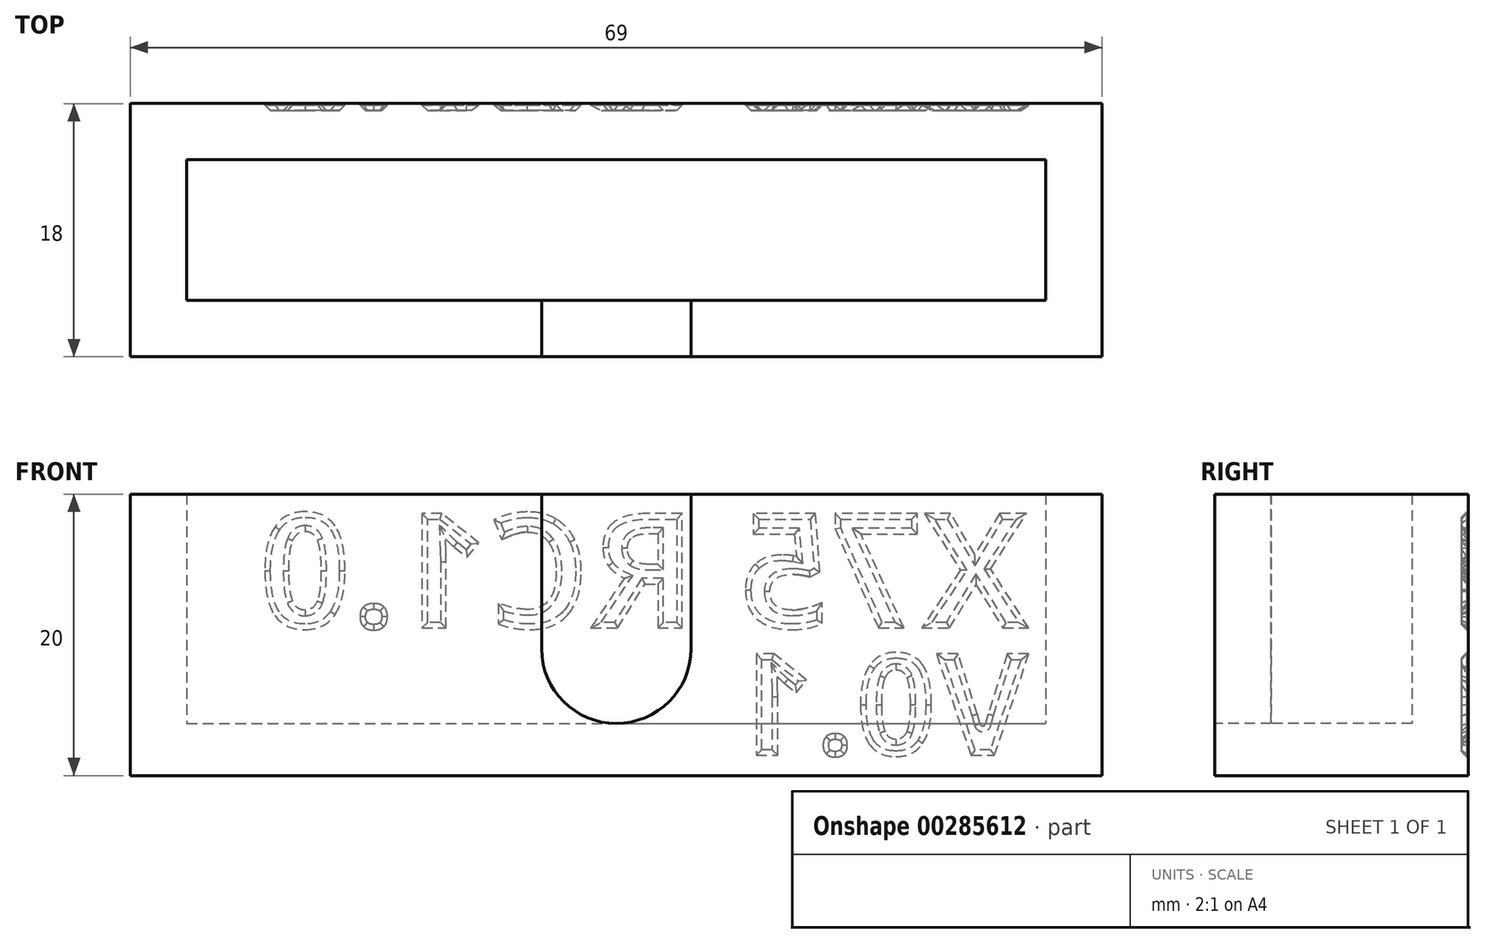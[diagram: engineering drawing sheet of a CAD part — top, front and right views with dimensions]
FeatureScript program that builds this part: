
annotation { "Feature Type Name" : "Feature", "Feature Type Description" : "" }
export const myFeature = defineFeature(function(context is Context, id is Id, definition is map)
    precondition{}
    {
        {
            var Q0;
            Q0=qCreatedBy(makeId("Top.planeOp"),FACE);
            var sketch = newSketch(context, id + "F0", { "sketchPlane" : qUnion([Q0])});
            skLineSegment(sketch, "E0.bottom", {"start": v(-31.49, -9.3) * mm, "end": v(37.51, -9.3) * mm});
            skLineSegment(sketch, "E0.top", {"start": v(-31.49, -27.3) * mm, "end": v(37.51, -27.3) * mm});
            skLineSegment(sketch, "E0.left", {"start": v(-31.49, -9.3) * mm, "end": v(-31.49, -27.3) * mm});
            skLineSegment(sketch, "E0.right", {"start": v(37.51, -9.3) * mm, "end": v(37.51, -27.3) * mm});
            skSolve(sketch);
        }
        {
            var Q0;
            Q0 = qSketchRegion(id + "F0", true);
            extrude(context, id + "F1", {"entities" : qUnion([Q0]), "depth" : 3.7 * mm});
        }
        {
            var Q0;
            Q0=makeQuery(id+"F1.opExtrude","CAP_FACE",FACE,{"disambiguationData":[OSD([sQuery(id+"F0.wireOp",EDGE,"E0.bottom"),sQuery(id+"F0.wireOp",EDGE,"E0.top"),sQuery(id+"F0.wireOp",EDGE,"E0.left"),sQuery(id+"F0.wireOp",EDGE,"E0.right")])],"isStart":false});
            var sketch = newSketch(context, id + "F2", { "sketchPlane" : qUnion([Q0])});
            skLineSegment(sketch, "E1.0.0", {"start": v(-31.49, -9.3) * mm, "end": v(-31.49, -27.3) * mm});
            skLineSegment(sketch, "E1.0.1", {"start": v(-31.49, -27.3) * mm, "end": v(37.51, -27.3) * mm});
            skLineSegment(sketch, "E1.0.2", {"start": v(37.51, -27.3) * mm, "end": v(37.51, -9.3) * mm});
            skLineSegment(sketch, "E1.0.3", {"start": v(37.51, -9.3) * mm, "end": v(-31.49, -9.3) * mm});
            skLineSegment(sketch, "E2.bottom", {"start": v(-27.49, -13.3) * mm, "end": v(33.51, -13.3) * mm});
            skLineSegment(sketch, "E2.top", {"start": v(-27.49, -23.3) * mm, "end": v(33.51, -23.3) * mm});
            skLineSegment(sketch, "E2.left", {"start": v(-27.49, -13.3) * mm, "end": v(-27.49, -23.3) * mm});
            skLineSegment(sketch, "E2.right", {"start": v(33.51, -13.3) * mm, "end": v(33.51, -23.3) * mm});
            skSolve(sketch);
        }
        {
            var Q0;
            Q0 = qSketchRegion(id + "F2", true);
            extrude(context, id + "F3", {"entities" : qUnion([Q0]), "operationType" : NewBodyOperationType.ADD, "depth" : (20 - 3.7) * mm});
        }
        {
            var Q0;
            Q0=makeQuery(id+"F3.boolean.opBoolean","MERGE",FACE,{"derivedFrom":[makeQuery(id+"F1.opExtrude","SWEPT_FACE",FACE,{"disambiguationData":[OSD([sQuery(id+"F0.wireOp",EDGE,"E0.top")])]}),makeQuery(id+"F3.opExtrude","SWEPT_FACE",FACE,{"disambiguationData":[OSD([sQuery(id+"F2.wireOp",EDGE,"E1.0.1")])]})]});
            var sketch = newSketch(context, id + "F4", { "sketchPlane" : qUnion([Q0])});
            skLineSegment(sketch, "E3", {"start": v(-31.49, 20) * mm, "end": v(-2.29, 20) * mm, "construction": true});
            skLineSegment(sketch, "E4", {"start": v(-2.29, 20) * mm, "end": v(8.31, 20) * mm});
            skLineSegment(sketch, "E5", {"start": v(-2.29, 20) * mm, "end": v(-2.29, 9) * mm});
            skLineSegment(sketch, "E6", {"start": v(3.01, 3.7) * mm, "end": v(3.01, 3.7) * mm});
            skLineSegment(sketch, "E7", {"start": v(8.31, 9) * mm, "end": v(8.31, 20) * mm});
            skPoint(sketch, "E8.visualSharp", {"position": v(-2.29, 3.7) * mm});
            skArc(sketch, "E8.filletArc", {"start": v(-2.29, 9) * mm, "mid": v(-0.73, 5.25) * mm, "end": v(3.01, 3.7) * mm});
            skPoint(sketch, "E9.visualSharp", {"position": v(8.31, 3.7) * mm});
            skArc(sketch, "E9.filletArc", {"start": v(3.01, 3.7) * mm, "mid": v(6.76, 5.25) * mm, "end": v(8.31, 9) * mm});
            skSolve(sketch);
        }
        {
            var Q0;
            Q0 = qSketchRegion(id + "F4", true);
            extrude(context, id + "F5", {"entities" : qUnion([Q0]), "operationType" : NewBodyOperationType.REMOVE, "oppositeDirection" : true, "depth" : 5 * mm});
        }
        {
            var Q0;
            Q0=makeQuery(id+"F3.boolean.opBoolean","MERGE",FACE,{"derivedFrom":[makeQuery(id+"F1.opExtrude","SWEPT_FACE",FACE,{"disambiguationData":[OSD([sQuery(id+"F0.wireOp",EDGE,"E0.bottom")])]}),makeQuery(id+"F3.opExtrude","SWEPT_FACE",FACE,{"disambiguationData":[OSD([sQuery(id+"F2.wireOp",EDGE,"E1.0.3")])]})]});
            var sketch = newSketch(context, id + "F6", { "sketchPlane" : qUnion([Q0])});
            skText(sketch, "E10", { "text": "X75 RC1.0 \n", "fontName": "OpenSans-Bold.ttf"});
            skText(sketch, "E11", { "text": "V0.1", "fontName": "OpenSans-Bold.ttf"});
            const initialGuessF6  = {"E10": [-0.0323, 0.01048, 1, 0, 0.00821], "E11": [-0.0323, 0.00144, 1, 0, 0.00726]};
            skSetInitialGuess(sketch, initialGuessF6);
            skSolve(sketch);
        }
        {
            var Q0;
            Q0 = qSketchRegion(id + "F6", true);
            extrude(context, id + "F7", {"entities" : qUnion([Q0]), "operationType" : NewBodyOperationType.REMOVE, "oppositeDirection" : true, "depth" : .5 * mm});
        }
        {
            var Q0;
            Q0=makeQuery(id+"F7.boolean.opBoolean","COPY",EDGE,{"derivedFrom":makeQuery(id+"F7.opExtrude","SWEPT_EDGE",EDGE,{"disambiguationData":[OSD([sQuery(id+"F6.wireOp",EDGE,"E11.sketch_text.stroke-7"),sQuery(id+"F6.wireOp",EDGE,"E11.sketch_text.stroke-8")])]})});
            fillet(context, id + "F8", {"entities" : qUnion([Q0]), "radius" : .2 * mm, "tangentPropagation" : true, "allowEdgeOverflow" : false});
        }
        {
            var Q0;
            Q0=makeQuery(id+"F7.boolean.opBoolean","COPY",FACE,{"derivedFrom":makeQuery(id+"F7.opExtrude","CAP_FACE",FACE,{"disambiguationData":[OSD([sQuery(id+"F6.wireOp",EDGE,"E10.sketch_text.stroke-0"),sQuery(id+"F6.wireOp",EDGE,"E10.sketch_text.stroke-1"),sQuery(id+"F6.wireOp",EDGE,"E10.sketch_text.stroke-2"),sQuery(id+"F6.wireOp",EDGE,"E10.sketch_text.stroke-3"),sQuery(id+"F6.wireOp",EDGE,"E10.sketch_text.stroke-4"),sQuery(id+"F6.wireOp",EDGE,"E10.sketch_text.stroke-5"),sQuery(id+"F6.wireOp",EDGE,"E10.sketch_text.stroke-6"),sQuery(id+"F6.wireOp",EDGE,"E10.sketch_text.stroke-7"),sQuery(id+"F6.wireOp",EDGE,"E10.sketch_text.stroke-8"),sQuery(id+"F6.wireOp",EDGE,"E10.sketch_text.stroke-9"),sQuery(id+"F6.wireOp",EDGE,"E10.sketch_text.stroke-10"),sQuery(id+"F6.wireOp",EDGE,"E10.sketch_text.stroke-11")])],"isStart":false})});
            var Q1;
            Q1=makeQuery(id+"F7.boolean.opBoolean","COPY",FACE,{"derivedFrom":makeQuery(id+"F7.opExtrude","CAP_FACE",FACE,{"disambiguationData":[OSD([sQuery(id+"F6.wireOp",EDGE,"E10.sketch_text.stroke-12"),sQuery(id+"F6.wireOp",EDGE,"E10.sketch_text.stroke-13"),sQuery(id+"F6.wireOp",EDGE,"E10.sketch_text.stroke-14"),sQuery(id+"F6.wireOp",EDGE,"E10.sketch_text.stroke-15"),sQuery(id+"F6.wireOp",EDGE,"E10.sketch_text.stroke-16"),sQuery(id+"F6.wireOp",EDGE,"E10.sketch_text.stroke-17"),sQuery(id+"F6.wireOp",EDGE,"E10.sketch_text.stroke-18")])],"isStart":false})});
            var Q2;
            Q2=makeQuery(id+"F7.boolean.opBoolean","COPY",FACE,{"derivedFrom":makeQuery(id+"F7.opExtrude","CAP_FACE",FACE,{"disambiguationData":[OSD([sQuery(id+"F6.wireOp",EDGE,"E10.sketch_text.stroke-19"),sQuery(id+"F6.wireOp",EDGE,"E10.sketch_text.stroke-20"),sQuery(id+"F6.wireOp",EDGE,"E10.sketch_text.stroke-21"),sQuery(id+"F6.wireOp",EDGE,"E10.sketch_text.stroke-22"),sQuery(id+"F6.wireOp",EDGE,"E10.sketch_text.stroke-23"),sQuery(id+"F6.wireOp",EDGE,"E10.sketch_text.stroke-24"),sQuery(id+"F6.wireOp",EDGE,"E10.sketch_text.stroke-25"),sQuery(id+"F6.wireOp",EDGE,"E10.sketch_text.stroke-26"),sQuery(id+"F6.wireOp",EDGE,"E10.sketch_text.stroke-27"),sQuery(id+"F6.wireOp",EDGE,"E10.sketch_text.stroke-28"),sQuery(id+"F6.wireOp",EDGE,"E10.sketch_text.stroke-29"),sQuery(id+"F6.wireOp",EDGE,"E10.sketch_text.stroke-30"),sQuery(id+"F6.wireOp",EDGE,"E10.sketch_text.stroke-31"),sQuery(id+"F6.wireOp",EDGE,"E10.sketch_text.stroke-32"),sQuery(id+"F6.wireOp",EDGE,"E10.sketch_text.stroke-33"),sQuery(id+"F6.wireOp",EDGE,"E10.sketch_text.stroke-34"),sQuery(id+"F6.wireOp",EDGE,"E10.sketch_text.stroke-35"),sQuery(id+"F6.wireOp",EDGE,"E10.sketch_text.stroke-36"),sQuery(id+"F6.wireOp",EDGE,"E10.sketch_text.stroke-37"),sQuery(id+"F6.wireOp",EDGE,"E10.sketch_text.stroke-38")])],"isStart":false})});
            var Q3;
            Q3=makeQuery(id+"F7.boolean.opBoolean","COPY",FACE,{"derivedFrom":makeQuery(id+"F7.opExtrude","CAP_FACE",FACE,{"disambiguationData":[OSD([sQuery(id+"F6.wireOp",EDGE,"E10.sketch_text.stroke-39"),sQuery(id+"F6.wireOp",EDGE,"E10.sketch_text.stroke-40"),sQuery(id+"F6.wireOp",EDGE,"E10.sketch_text.stroke-41"),sQuery(id+"F6.wireOp",EDGE,"E10.sketch_text.stroke-42"),sQuery(id+"F6.wireOp",EDGE,"E10.sketch_text.stroke-43"),sQuery(id+"F6.wireOp",EDGE,"E10.sketch_text.stroke-44"),sQuery(id+"F6.wireOp",EDGE,"E10.sketch_text.stroke-45"),sQuery(id+"F6.wireOp",EDGE,"E10.sketch_text.stroke-46"),sQuery(id+"F6.wireOp",EDGE,"E10.sketch_text.stroke-47"),sQuery(id+"F6.wireOp",EDGE,"E10.sketch_text.stroke-48"),sQuery(id+"F6.wireOp",EDGE,"E10.sketch_text.stroke-49"),sQuery(id+"F6.wireOp",EDGE,"E10.sketch_text.stroke-50"),sQuery(id+"F6.wireOp",EDGE,"E10.sketch_text.stroke-51"),sQuery(id+"F6.wireOp",EDGE,"E10.sketch_text.stroke-52"),sQuery(id+"F6.wireOp",EDGE,"E10.sketch_text.stroke-53"),sQuery(id+"F6.wireOp",EDGE,"E10.sketch_text.stroke-54"),sQuery(id+"F6.wireOp",EDGE,"E10.sketch_text.stroke-55"),sQuery(id+"F6.wireOp",EDGE,"E10.sketch_text.stroke-56"),sQuery(id+"F6.wireOp",EDGE,"E10.sketch_text.stroke-57")])],"isStart":false})});
            var Q4;
            Q4=makeQuery(id+"F7.boolean.opBoolean","COPY",FACE,{"derivedFrom":makeQuery(id+"F7.opExtrude","CAP_FACE",FACE,{"disambiguationData":[OSD([sQuery(id+"F6.wireOp",EDGE,"E10.sketch_text.stroke-58"),sQuery(id+"F6.wireOp",EDGE,"E10.sketch_text.stroke-59"),sQuery(id+"F6.wireOp",EDGE,"E10.sketch_text.stroke-60"),sQuery(id+"F6.wireOp",EDGE,"E10.sketch_text.stroke-61"),sQuery(id+"F6.wireOp",EDGE,"E10.sketch_text.stroke-62"),sQuery(id+"F6.wireOp",EDGE,"E10.sketch_text.stroke-63"),sQuery(id+"F6.wireOp",EDGE,"E10.sketch_text.stroke-64"),sQuery(id+"F6.wireOp",EDGE,"E10.sketch_text.stroke-65"),sQuery(id+"F6.wireOp",EDGE,"E10.sketch_text.stroke-66"),sQuery(id+"F6.wireOp",EDGE,"E10.sketch_text.stroke-67"),sQuery(id+"F6.wireOp",EDGE,"E10.sketch_text.stroke-68"),sQuery(id+"F6.wireOp",EDGE,"E10.sketch_text.stroke-69"),sQuery(id+"F6.wireOp",EDGE,"E10.sketch_text.stroke-70"),sQuery(id+"F6.wireOp",EDGE,"E10.sketch_text.stroke-71"),sQuery(id+"F6.wireOp",EDGE,"E10.sketch_text.stroke-72")])],"isStart":false})});
            var Q5;
            Q5=makeQuery(id+"F7.boolean.opBoolean","COPY",FACE,{"derivedFrom":makeQuery(id+"F7.opExtrude","CAP_FACE",FACE,{"disambiguationData":[OSD([sQuery(id+"F6.wireOp",EDGE,"E10.sketch_text.stroke-73"),sQuery(id+"F6.wireOp",EDGE,"E10.sketch_text.stroke-74"),sQuery(id+"F6.wireOp",EDGE,"E10.sketch_text.stroke-75"),sQuery(id+"F6.wireOp",EDGE,"E10.sketch_text.stroke-76"),sQuery(id+"F6.wireOp",EDGE,"E10.sketch_text.stroke-77"),sQuery(id+"F6.wireOp",EDGE,"E10.sketch_text.stroke-78"),sQuery(id+"F6.wireOp",EDGE,"E10.sketch_text.stroke-79"),sQuery(id+"F6.wireOp",EDGE,"E10.sketch_text.stroke-80"),sQuery(id+"F6.wireOp",EDGE,"E10.sketch_text.stroke-81"),sQuery(id+"F6.wireOp",EDGE,"E10.sketch_text.stroke-82")])],"isStart":false})});
            var Q6;
            Q6=makeQuery(id+"F7.boolean.opBoolean","COPY",FACE,{"derivedFrom":makeQuery(id+"F7.opExtrude","CAP_FACE",FACE,{"disambiguationData":[OSD([sQuery(id+"F6.wireOp",EDGE,"E10.sketch_text.stroke-83"),sQuery(id+"F6.wireOp",EDGE,"E10.sketch_text.stroke-84"),sQuery(id+"F6.wireOp",EDGE,"E10.sketch_text.stroke-85"),sQuery(id+"F6.wireOp",EDGE,"E10.sketch_text.stroke-86"),sQuery(id+"F6.wireOp",EDGE,"E10.sketch_text.stroke-87"),sQuery(id+"F6.wireOp",EDGE,"E10.sketch_text.stroke-88"),sQuery(id+"F6.wireOp",EDGE,"E10.sketch_text.stroke-89"),sQuery(id+"F6.wireOp",EDGE,"E10.sketch_text.stroke-90")])],"isStart":false})});
            var Q7;
            Q7=makeQuery(id+"F7.boolean.opBoolean","COPY",FACE,{"derivedFrom":makeQuery(id+"F7.opExtrude","CAP_FACE",FACE,{"disambiguationData":[OSD([sQuery(id+"F6.wireOp",EDGE,"E10.sketch_text.stroke-91"),sQuery(id+"F6.wireOp",EDGE,"E10.sketch_text.stroke-92"),sQuery(id+"F6.wireOp",EDGE,"E10.sketch_text.stroke-93"),sQuery(id+"F6.wireOp",EDGE,"E10.sketch_text.stroke-94"),sQuery(id+"F6.wireOp",EDGE,"E10.sketch_text.stroke-95"),sQuery(id+"F6.wireOp",EDGE,"E10.sketch_text.stroke-96"),sQuery(id+"F6.wireOp",EDGE,"E10.sketch_text.stroke-97"),sQuery(id+"F6.wireOp",EDGE,"E10.sketch_text.stroke-98"),sQuery(id+"F6.wireOp",EDGE,"E10.sketch_text.stroke-99"),sQuery(id+"F6.wireOp",EDGE,"E10.sketch_text.stroke-100"),sQuery(id+"F6.wireOp",EDGE,"E10.sketch_text.stroke-101"),sQuery(id+"F6.wireOp",EDGE,"E10.sketch_text.stroke-102"),sQuery(id+"F6.wireOp",EDGE,"E10.sketch_text.stroke-103"),sQuery(id+"F6.wireOp",EDGE,"E10.sketch_text.stroke-104"),sQuery(id+"F6.wireOp",EDGE,"E10.sketch_text.stroke-105"),sQuery(id+"F6.wireOp",EDGE,"E10.sketch_text.stroke-106")])],"isStart":false})});
            var Q8;
            Q8=makeQuery(id+"F7.boolean.opBoolean","COPY",FACE,{"derivedFrom":makeQuery(id+"F7.opExtrude","CAP_FACE",FACE,{"disambiguationData":[OSD([sQuery(id+"F6.wireOp",EDGE,"E11.sketch_text.stroke-34"),sQuery(id+"F6.wireOp",EDGE,"E11.sketch_text.stroke-35"),sQuery(id+"F6.wireOp",EDGE,"E11.sketch_text.stroke-36"),sQuery(id+"F6.wireOp",EDGE,"E11.sketch_text.stroke-37"),sQuery(id+"F6.wireOp",EDGE,"E11.sketch_text.stroke-38"),sQuery(id+"F6.wireOp",EDGE,"E11.sketch_text.stroke-39"),sQuery(id+"F6.wireOp",EDGE,"E11.sketch_text.stroke-40"),sQuery(id+"F6.wireOp",EDGE,"E11.sketch_text.stroke-41"),sQuery(id+"F6.wireOp",EDGE,"E11.sketch_text.stroke-42"),sQuery(id+"F6.wireOp",EDGE,"E11.sketch_text.stroke-43")])],"isStart":false})});
            var Q9;
            Q9=makeQuery(id+"F7.boolean.opBoolean","COPY",FACE,{"derivedFrom":makeQuery(id+"F7.opExtrude","CAP_FACE",FACE,{"disambiguationData":[OSD([sQuery(id+"F6.wireOp",EDGE,"E11.sketch_text.stroke-26"),sQuery(id+"F6.wireOp",EDGE,"E11.sketch_text.stroke-27"),sQuery(id+"F6.wireOp",EDGE,"E11.sketch_text.stroke-28"),sQuery(id+"F6.wireOp",EDGE,"E11.sketch_text.stroke-29"),sQuery(id+"F6.wireOp",EDGE,"E11.sketch_text.stroke-30"),sQuery(id+"F6.wireOp",EDGE,"E11.sketch_text.stroke-31"),sQuery(id+"F6.wireOp",EDGE,"E11.sketch_text.stroke-32"),sQuery(id+"F6.wireOp",EDGE,"E11.sketch_text.stroke-33")])],"isStart":false})});
            var Q10;
            Q10=makeQuery(id+"F7.boolean.opBoolean","COPY",FACE,{"derivedFrom":makeQuery(id+"F7.opExtrude","CAP_FACE",FACE,{"disambiguationData":[OSD([sQuery(id+"F6.wireOp",EDGE,"E11.sketch_text.stroke-10"),sQuery(id+"F6.wireOp",EDGE,"E11.sketch_text.stroke-11"),sQuery(id+"F6.wireOp",EDGE,"E11.sketch_text.stroke-12"),sQuery(id+"F6.wireOp",EDGE,"E11.sketch_text.stroke-13"),sQuery(id+"F6.wireOp",EDGE,"E11.sketch_text.stroke-14"),sQuery(id+"F6.wireOp",EDGE,"E11.sketch_text.stroke-15"),sQuery(id+"F6.wireOp",EDGE,"E11.sketch_text.stroke-16"),sQuery(id+"F6.wireOp",EDGE,"E11.sketch_text.stroke-17"),sQuery(id+"F6.wireOp",EDGE,"E11.sketch_text.stroke-18"),sQuery(id+"F6.wireOp",EDGE,"E11.sketch_text.stroke-19"),sQuery(id+"F6.wireOp",EDGE,"E11.sketch_text.stroke-20"),sQuery(id+"F6.wireOp",EDGE,"E11.sketch_text.stroke-21"),sQuery(id+"F6.wireOp",EDGE,"E11.sketch_text.stroke-22"),sQuery(id+"F6.wireOp",EDGE,"E11.sketch_text.stroke-23"),sQuery(id+"F6.wireOp",EDGE,"E11.sketch_text.stroke-24"),sQuery(id+"F6.wireOp",EDGE,"E11.sketch_text.stroke-25")])],"isStart":false})});
            var Q11;
            Q11=makeQuery(id+"F7.boolean.opBoolean","COPY",FACE,{"derivedFrom":makeQuery(id+"F7.opExtrude","CAP_FACE",FACE,{"disambiguationData":[OSD([sQuery(id+"F6.wireOp",EDGE,"E11.sketch_text.stroke-0"),sQuery(id+"F6.wireOp",EDGE,"E11.sketch_text.stroke-1"),sQuery(id+"F6.wireOp",EDGE,"E11.sketch_text.stroke-2"),sQuery(id+"F6.wireOp",EDGE,"E11.sketch_text.stroke-3"),sQuery(id+"F6.wireOp",EDGE,"E11.sketch_text.stroke-4"),sQuery(id+"F6.wireOp",EDGE,"E11.sketch_text.stroke-5"),sQuery(id+"F6.wireOp",EDGE,"E11.sketch_text.stroke-6"),sQuery(id+"F6.wireOp",EDGE,"E11.sketch_text.stroke-7"),sQuery(id+"F6.wireOp",EDGE,"E11.sketch_text.stroke-8"),sQuery(id+"F6.wireOp",EDGE,"E11.sketch_text.stroke-9")])],"isStart":false})});
            chamfer(context, id + "F9", {"entities" : qUnion([Q0, Q1, Q2, Q3, Q4, Q5, Q6, Q7, Q8, Q9, Q10, Q11]), "width" : .4 * mm, "tangentPropagation" : true});
        }
    });
